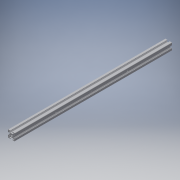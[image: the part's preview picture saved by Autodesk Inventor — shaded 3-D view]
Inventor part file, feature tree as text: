
AUTODESK INVENTOR PART (.ipt)
format: ipt  version: 2017 (Build 210142000, 142)  size: 439,296 bytes
history: native  units: in
note: dims shown in document units (in); Inventor stores cm internally (conversion verified against a paired STEP export)
features: other x3, extrude x2, sketch x2, projected_geometry x2
ambient origin geometry x8: Origin, YZ Plane, XZ Plane, XY Plane, X Axis, Y Axis, Z Axis, Center Point
bodies: Solid1 (feature_tree)
feature tree (9):
  other  "Blocks"
  extrude  "Extrusion1"  Depth=17.5in
  extrude  "Extrusion3"  Depth=0.2in
  sketch  "Sketch1"  dims[d1=0.0in d5=17.5in]
  other  "20x20"
  sketch  "Sketch3"  dims[d6=0.2953in d9=0.2in d10=0.1476in d11=4.75in d12=0.2in d13=0.1476in d14=8.75in d15=0.2in d16=0.1476in d17=4.75in d18=1.0in d19=0.0in]
  projected_geometry  "Projected Loop1"
  projected_geometry  "Projected Loop2"
  other  "20x20:1"
